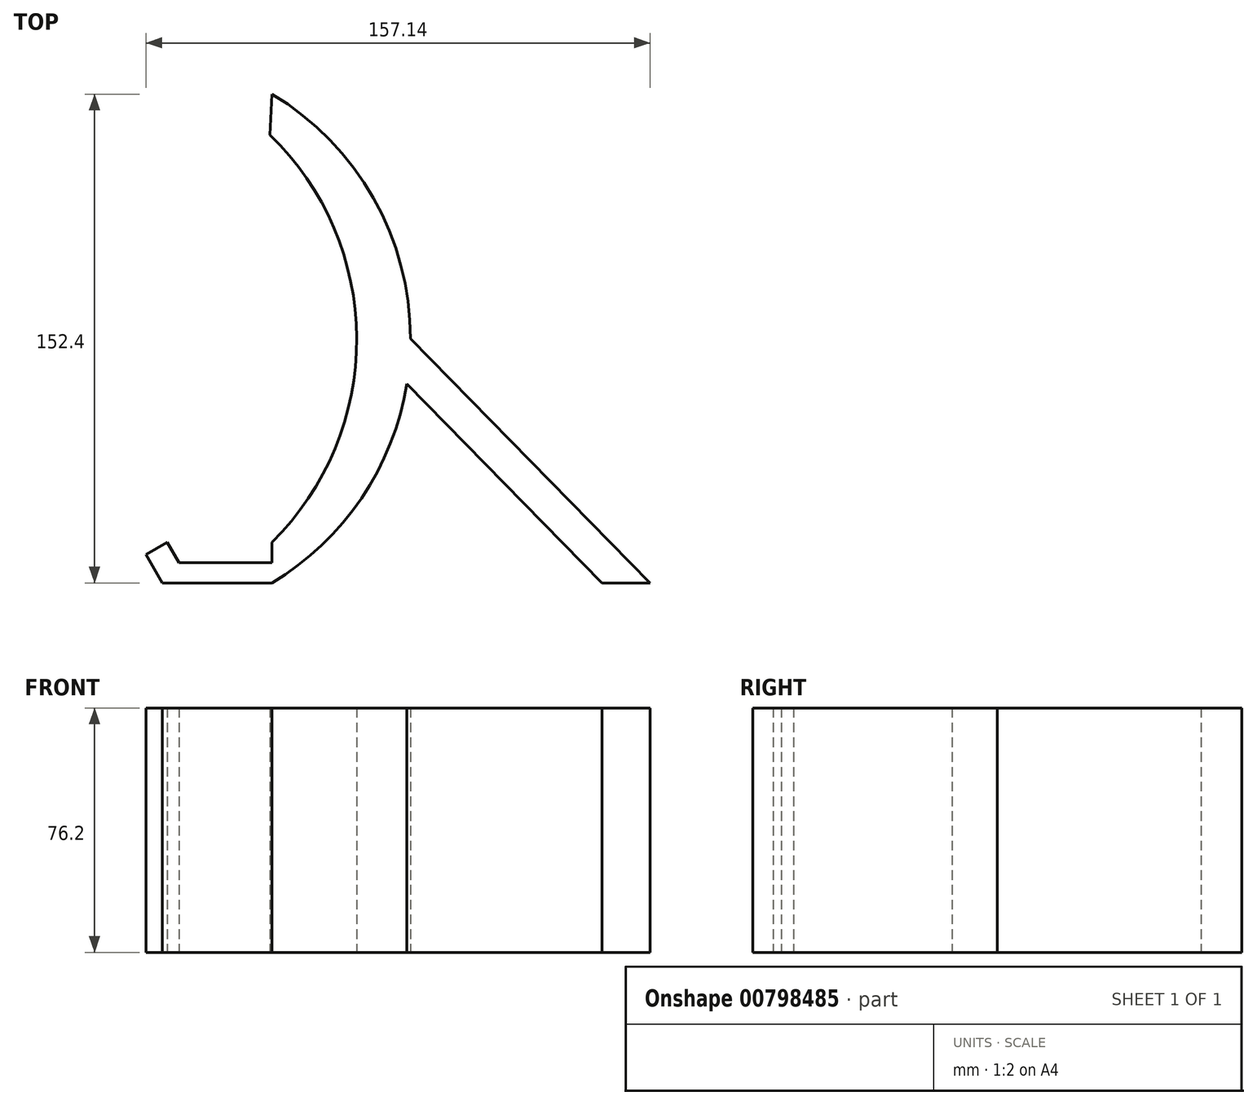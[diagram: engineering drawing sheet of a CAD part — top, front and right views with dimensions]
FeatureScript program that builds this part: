
annotation { "Feature Type Name" : "Feature", "Feature Type Description" : "" }
export const myFeature = defineFeature(function(context is Context, id is Id, definition is map)
    precondition{}
    {
        {
            var Q0;
            Q0=qCreatedBy(makeId("Top.planeOp"),FACE);
            var sketch = newSketch(context, id + "F0", { "sketchPlane" : qUnion([Q0])});
            skLineSegment(sketch, "E0", {"start": v(0, 0) * mm, "end": v(-25.4, 0) * mm});
            skLineSegment(sketch, "E1", {"start": v(-25.4, 0) * mm, "end": v(-32.73, 12.7) * mm});
            skLineSegment(sketch, "E2", {"start": v(0, 0) * mm, "end": v(0, 139.7) * mm, "construction": true});
            skArc(sketch, "E3", {"start": v(0, 0) * mm, "mid": v(43.1, 76.2) * mm, "end": v(0, 152.4) * mm});
            skLineSegment(sketch, "E4", {"start": v(0, 0) * mm, "end": v(0, 12.7) * mm, "construction": true});
            skLineSegment(sketch, "E5", {"start": v(-0.64, 139.7) * mm, "end": v(4.22, 236.77) * mm, "construction": true});
            skLineSegment(sketch, "E6", {"start": v(0, 152.4) * mm, "end": v(-0.64, 139.7) * mm});
            skPoint(sketch, "E7.orphan", {"position": v(-7.62, 0) * mm});
            skArc(sketch, "E8", {"start": v(0, 12.7) * mm, "mid": v(26.37, 76.33) * mm, "end": v(-0.63, 139.7) * mm});
            skLineSegment(sketch, "E9", {"start": v(0, 6.35) * mm, "end": v(-29.07, 6.35) * mm});
            skLineSegment(sketch, "E10", {"start": v(-32.73, 12.7) * mm, "end": v(-39.35, 8.88) * mm});
            skLineSegment(sketch, "E11", {"start": v(-39.35, 8.88) * mm, "end": v(-34.22, 0) * mm});
            skLineSegment(sketch, "E12", {"start": v(-34.22, 0) * mm, "end": v(-25.4, 0) * mm});
            skLineSegment(sketch, "E13", {"start": v(0, 6.35) * mm, "end": v(0, 12.7) * mm});
            skLineSegment(sketch, "E14", {"start": v(43.1, 76.2) * mm, "end": v(117.8, 0) * mm});
            skLineSegment(sketch, "E15", {"start": v(102.85, 0) * mm, "end": v(41.98, 62.1) * mm});
            skLineSegment(sketch, "E16", {"start": v(102.85, 0) * mm, "end": v(117.8, 0) * mm});
            skLineSegment(sketch, "E17.bottom", {"start": v(-45.38, -5.4) * mm, "end": v(121.72, -5.4) * mm});
            skLineSegment(sketch, "E17.top", {"start": v(-45.38, 160.45) * mm, "end": v(121.72, 160.45) * mm});
            skLineSegment(sketch, "E17.left", {"start": v(-45.38, -5.4) * mm, "end": v(-45.38, 160.45) * mm});
            skLineSegment(sketch, "E17.right", {"start": v(121.72, -5.4) * mm, "end": v(121.72, 160.45) * mm});
            skSolve(sketch);
        }
        {
            var Q0;
            {var subQ0=sQuery(id+"F0.wireOp",EDGE,"E10");Q0=makeQuery(id+"F0.imprint","IMPRINT",FACE,{"disambiguationData":[TD([[makeQuery(id+"F0.imprint","IMPRINT",EDGE,{"derivedFrom":subQ0}),1.0]])]});}
            var Q1;
            {var subQ1=sQuery(id+"F0.wireOp",EDGE,"E0");Q1=makeQuery(id+"F0.imprint","IMPRINT",FACE,{"disambiguationData":[TD([[makeQuery(id+"F0.imprint","IMPRINT",EDGE,{"derivedFrom":subQ1}),-1.0]])]});}
            var Q2;
            {var subQ0=sQuery(id+"F0.wireOp",EDGE,"E14");Q2=makeQuery(id+"F0.imprint","IMPRINT",FACE,{"disambiguationData":[TD([[makeQuery(id+"F0.imprint","IMPRINT",EDGE,{"derivedFrom":subQ0}),-1.0]])]});}
            extrude(context, id + "F1", {"entities" : qUnion([Q0, Q1, Q2]), "depth" : 76.2 * mm, "offsetDistance" : 25.4 * mm});
        }
    });
